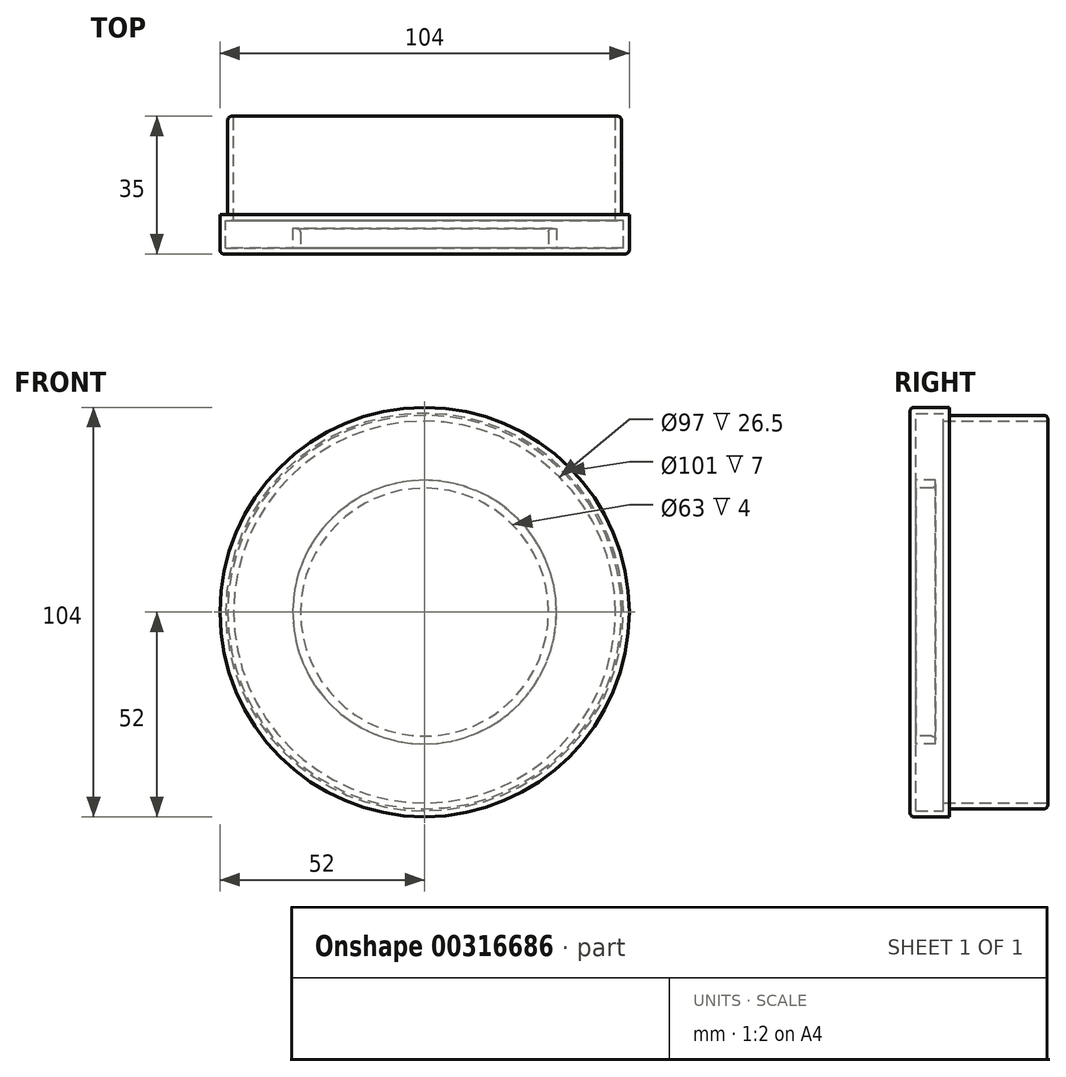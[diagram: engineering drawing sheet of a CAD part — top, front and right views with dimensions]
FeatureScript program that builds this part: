
annotation { "Feature Type Name" : "Feature", "Feature Type Description" : "" }
export const myFeature = defineFeature(function(context is Context, id is Id, definition is map)
    precondition{}
    {
        {
            var Q0;
            Q0=qCreatedBy(makeId("Front.planeOp"),FACE);
            var sketch = newSketch(context, id + "F0", { "sketchPlane" : qUnion([Q0])});
            skCircle(sketch, "E0", {"center": v(0, 0) * mm, "radius": 50 * mm});
            skSolve(sketch);
        }
        {
            var Q0;
            Q0=makeQuery(id+"F0.imprint","IMPRINT",FACE,{"disambiguationData":[TD([[makeQuery(id+"F0.imprint","IMPRINT",EDGE,{"derivedFrom":sQuery(id+"F0.wireOp",EDGE,"E0")}),1.0]])]});
            extrude(context, id + "F1", {"entities" : qUnion([Q0]), "depth" : 25 * mm});
        }
        {
            var Q0;
            Q0=makeQuery(id+"F1.opExtrude","CAP_FACE",FACE,{"disambiguationData":[OSD([sQuery(id+"F0.wireOp",EDGE,"E0")])],"isStart":false});
            var sketch = newSketch(context, id + "F2", { "sketchPlane" : qUnion([Q0])});
            skCircle(sketch, "E1", {"center": v(0, 0) * mm, "radius": 52 * mm});
            skSolve(sketch);
        }
        {
            var Q0;
            Q0=makeQuery(id+"F2.imprint","IMPRINT",FACE,{"disambiguationData":[TD([[makeQuery(id+"F2.imprint","IMPRINT",EDGE,{"derivedFrom":sQuery(id+"F2.wireOp",EDGE,"E1")}),1.0]])]});
            var Q1;
            Q1=makeQuery(id+"F2.imprint","IMPRINT",FACE,{"disambiguationData":[TD([[makeQuery(id+"F2.imprint","IMPRINT",EDGE,{"derivedFrom":makeQuery(id+"F1.opExtrude","CAP_EDGE",EDGE,{"disambiguationData":[OSD([sQuery(id+"F0.wireOp",EDGE,"E0")])],"isStart":false})}),1.0]])]});
            extrude(context, id + "F3", {"entities" : qUnion([Q0, Q1]), "operationType" : NewBodyOperationType.ADD, "depth" : 10 * mm});
        }
        {
            var Q0;
            Q0=makeQuery(id+"F3.opExtrude","CAP_EDGE",EDGE,{"disambiguationData":[OSD([sQuery(id+"F2.wireOp",EDGE,"E1")])],"isStart":false});
            var Q1;
            Q1=makeQuery(id+"F1.opExtrude","CAP_EDGE",EDGE,{"disambiguationData":[OSD([sQuery(id+"F0.wireOp",EDGE,"E0")])],"isStart":true});
            fillet(context, id + "F4", {"entities" : qUnion([Q0, Q1]), "radius" : 1 * mm, "tangentPropagation" : true, "allowEdgeOverflow" : false});
        }
        {
            var Q0;
            Q0=makeQuery(id+"F1.opExtrude","CAP_FACE",FACE,{"disambiguationData":[OSD([sQuery(id+"F0.wireOp",EDGE,"E0")])],"isStart":true});
            shell(context, id + "F5", {"entities" : qUnion([Q0]), "thickness" : 1.5 * mm});
        }
        {
            var Q0;
            {var subQ0=sQuery(id+"F2.wireOp",EDGE,"E1");Q0=makeQuery(id+"F5.opShell","OFFSET_FACE",FACE,{"disambiguationData":[OSD([subQ0]),TDD([makeQuery(id+"F3.opExtrude","CAP_FACE",FACE,{"disambiguationData":[OSD([subQ0])],"isStart":false})])]});}
            var sketch = newSketch(context, id + "F6", { "sketchPlane" : qUnion([Q0])});
            skCircle(sketch, "E2", {"center": v(0, 0) * mm, "radius": 31.5 * mm});
            skCircle(sketch, "E3", {"center": v(0, 0) * mm, "radius": 33.5 * mm});
            skSolve(sketch);
        }
        {
            var Q0;
            Q0=makeQuery(id+"F6.imprint","IMPRINT",FACE,{"disambiguationData":[TD([[makeQuery(id+"F6.imprint","IMPRINT",EDGE,{"derivedFrom":sQuery(id+"F6.wireOp",EDGE,"E2")}),-1.0]])]});
            extrude(context, id + "F7", {"entities" : qUnion([Q0]), "operationType" : NewBodyOperationType.ADD, "depth" : 5 * mm});
        }
        {
            var Q0;
            Q0=makeQuery(id+"F7.opExtrude","CAP_EDGE",EDGE,{"disambiguationData":[OSD([sQuery(id+"F6.wireOp",EDGE,"E2")])],"isStart":false});
            fillet(context, id + "F8", {"entities" : qUnion([Q0]), "radius" : 1 * mm, "tangentPropagation" : true, "allowEdgeOverflow" : false});
        }
    });
